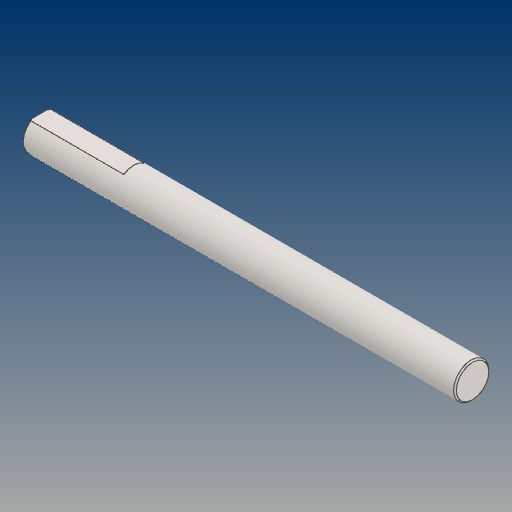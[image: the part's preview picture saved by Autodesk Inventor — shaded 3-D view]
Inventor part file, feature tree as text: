
AUTODESK INVENTOR PART (.ipt)
format: ipt  version: 2021 (Build 250183000, 183)  size: 95,232 bytes
history: native  units: mm
features: chamfer x1
ambient origin geometry x8: Origin, YZ Plane, XZ Plane, XY Plane, X Axis, Y Axis, Z Axis, Center Point
bodies: Solid1 (feature_tree)
feature tree (1):
  chamfer  "Chamfer1"  [1 undecoded]
note: 1 required parameter value undecoded (feature->parameter linkage not recoverable at this tier; creation-order binding heuristic only, values carry confidence <= 0.55)
